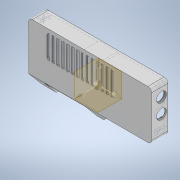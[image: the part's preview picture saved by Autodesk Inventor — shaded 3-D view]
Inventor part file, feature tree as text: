
AUTODESK INVENTOR PART (.ipt)
format: ipt  version: 2021 (Build 250183000, 183)  size: 589,824 bytes
history: native  units: mm
features: sketch x24, extrude x23, chamfer x7, fillet x5, hole x1
ambient origin geometry x8: Origin, YZ Plane, XZ Plane, XY Plane, X Axis, Y Axis, Z Axis, Center Point
bodies: Solid1 (feature_tree)
feature tree (60):
  extrude  "Extrusion1"  Depth=100.0mm
  extrude  "Extrusion3"  Depth=50.0mm
  extrude  "Extrusion4"  Depth=1.2mm
  extrude  "Extrusion12"  Depth=3.0mm TaperAngle=0.0deg
  extrude  "Extrusion13"  Depth=3.0mm TaperAngle=0.0deg
  fillet  "Fillet3"  Radius=2.0mm
  extrude  "Extrusion15"  Depth=2.0mm
  extrude  "Extrusion20"  Depth=44.0mm
  extrude  "Extrusion21"  Depth=12.0mm TaperAngle=0.0deg
  extrude  "Extrusion22"  Depth=2.0mm
  extrude  "Extrusion23"  Depth=3.0mm
  extrude  "Extrusion26"  Depth=4.4mm TaperAngle=0.0deg
  hole  "Hole2"  [1 undecoded]
  chamfer  "Chamfer3"  Distance=12.0mm
  chamfer  "Chamfer4"  Distance=12.0mm
  chamfer  "Chamfer5"  Distance=2.0mm
  chamfer  "Chamfer6"  Distance=2.0mm
  chamfer  "Chamfer7"  Distance=3.0mm
  extrude  "Extrusion27"  Depth=2.0mm
  fillet  "Fillet4"  Radius=97.0mm
  extrude  "Extrusion28"  Depth=2.0mm
  extrude  "Extrusion29"  Depth=3.0mm
  extrude  "Extrusion30"  Depth=3.0mm
  fillet  "Fillet5"  Radius=97.0mm
  extrude  "Extrusion34"  Depth=2.0mm
  extrude  "Extrusion35"  Depth=2.0mm
  extrude  "Extrusion36"  Depth=2.0mm
  extrude  "Extrusion37"  Depth=2.0mm
  fillet  "Fillet6"  Radius=4.8mm
  extrude  "Extrusion38"  Depth=2.0mm
  extrude  "Extrusion39"  Depth=2.0mm TaperAngle=0.0deg
  chamfer  "Chamfer8"  Distance=2.0mm Angle=45.0deg
  extrude  "Extrusion40"  Depth=1.0mm TaperAngle=45.0deg
  fillet  "Fillet7"  Radius=2.0mm
  extrude  "Extrusion41"  Depth=2.0mm TaperAngle=45.0deg
  chamfer  "Chamfer9"  Distance=0.8mm Angle=45.0deg
  sketch  "Sketch1"  dims[d0=52.0mm d1=100.0mm]
  sketch  "Sketch4"  dims[d2=26.0mm d3=50.0mm]
  sketch  "Sketch5"  dims[d4=1.2mm d5=0.0mm d35=12.5mm]
  sketch  "Sketch13"  dims[d36=63.1mm d37=3.0mm d38=0.0mm]
  sketch  "Sketch14"  dims[d39=50.673mm d40=3.0mm d41=0.0mm d79=2.0mm]
  sketch  "Sketch16"  dims[d80=2.0mm d81=2.0mm]
  sketch  "Sketch21"  dims[d82=1.2mm d83=44.0mm]
  sketch  "Sketch22"  dims[d84=59.0mm d85=12.0mm d86=0.0mm]
  sketch  "Sketch23"  dims[d87=2.0mm d88=12.6mm]
  sketch  "Sketch24"  dims[d89=12.0mm d90=0.0mm d91=3.0mm]
  sketch  "Sketch27"  dims[d95=33.8mm d96=4.4mm d97=0.0mm]
  sketch  "Sketch28"  dims[d117=2.0mm d118=2.0mm d119=12.0mm d120=0.0mm d121=12.0mm d122=0.0mm]
  sketch  "Sketch29"  dims[d123=70.0mm]
  sketch  "Sketch30"  dims[d124=89.0mm]
  sketch  "Sketch31"  dims[d125=8.0mm]
  sketch  "Sketch32"  dims[d126=8.0mm d127=2.0mm d128=0.0mm]
  sketch  "Sketch36"  dims[d129=8.0mm]
  sketch  "Sketch37"  dims[d130=10.0mm]
  sketch  "Sketch38"  dims[d131=12.0mm]
  sketch  "Sketch39"  dims[d132=8.0mm]
  sketch  "Sketch40"  dims[d133=8.0mm]
  sketch  "Sketch41"  dims[d134=8.0mm d135=2.0mm d136=0.0mm]
  sketch  "Sketch43"  dims[d144=3.0mm]
  sketch  "Sketch45"  dims[d145=3.0mm d146=3.0mm d147=50.0mm d148=97.0mm d149=15.0mm d150=3.0mm d151=3.0mm d152=97.0mm d153=49.0mm d154=4.8mm d155=4.8mm d156=4.8mm d157=4.8mm d158=4.8mm d159=5.0mm d160=0.0mm d161=2.0mm d162=6.0mm d163=4.0mm d164=2.0mm d165=90.0deg d166=4.0mm d167=20.594885mm d168=2.0mm d169=2.0mm d170=45.0deg d171=1.0mm d172=2.0mm d173=45.0deg d174=2.0mm d175=2.0mm d176=45.0deg d177=2.0mm d178=2.0mm d179=45.0deg d180=0.8mm d181=2.0mm d182=45.0deg d184=68.0mm d189=2.0mm d190=0.0mm d191=2.0mm d192=2.0mm d193=24.0mm d194=2.0mm d195=0.0mm d196=36.5mm d197=46.5mm d198=3.5mm d199=2.0mm d200=0.0mm d201=12.5mm d202=23.0mm d203=3.5mm d204=2.0mm d205=0.0mm d206=1.0mm d217=7.6mm d218=10.0mm d219=46.4mm d220=20.0mm d221=0.0mm d222=22.68928mm d223=67.0mm d224=0.0mm d225=1.2mm d226=0.0mm d227=1.2mm d228=0.0mm d229=3.0mm d230=12.3mm d231=33.2mm d232=1.0mm d233=10.0mm d234=1.2mm d235=0.0mm d236=1.2mm d237=5.0mm d238=20.0mm d239=1.5mm d240=0.0mm d241=1.5mm d242=2.0mm d243=45.0deg d245=2.711255mm d246=12.0mm d247=33.2mm d248=3.0mm d249=0.0mm d251=2.0mm d252=1.2mm d253=10.0mm d254=1.5mm d255=0.0mm d256=1.5mm d257=2.0mm d258=45.0deg d67=0.5mm d68=0.872665mm d69=0.5mm d70=0.872665mm d71=0.5mm d72=0.872665mm d73=0.5mm d74=0.872665mm d75=0.872665mm d76=0.5mm d77=0.872665mm d208=0.5mm d209=0.872665mm d210=0.5mm d211=0.872665mm]
note: 1 required parameter value undecoded (feature->parameter linkage not recoverable at this tier; creation-order binding heuristic only, values carry confidence <= 0.55)
